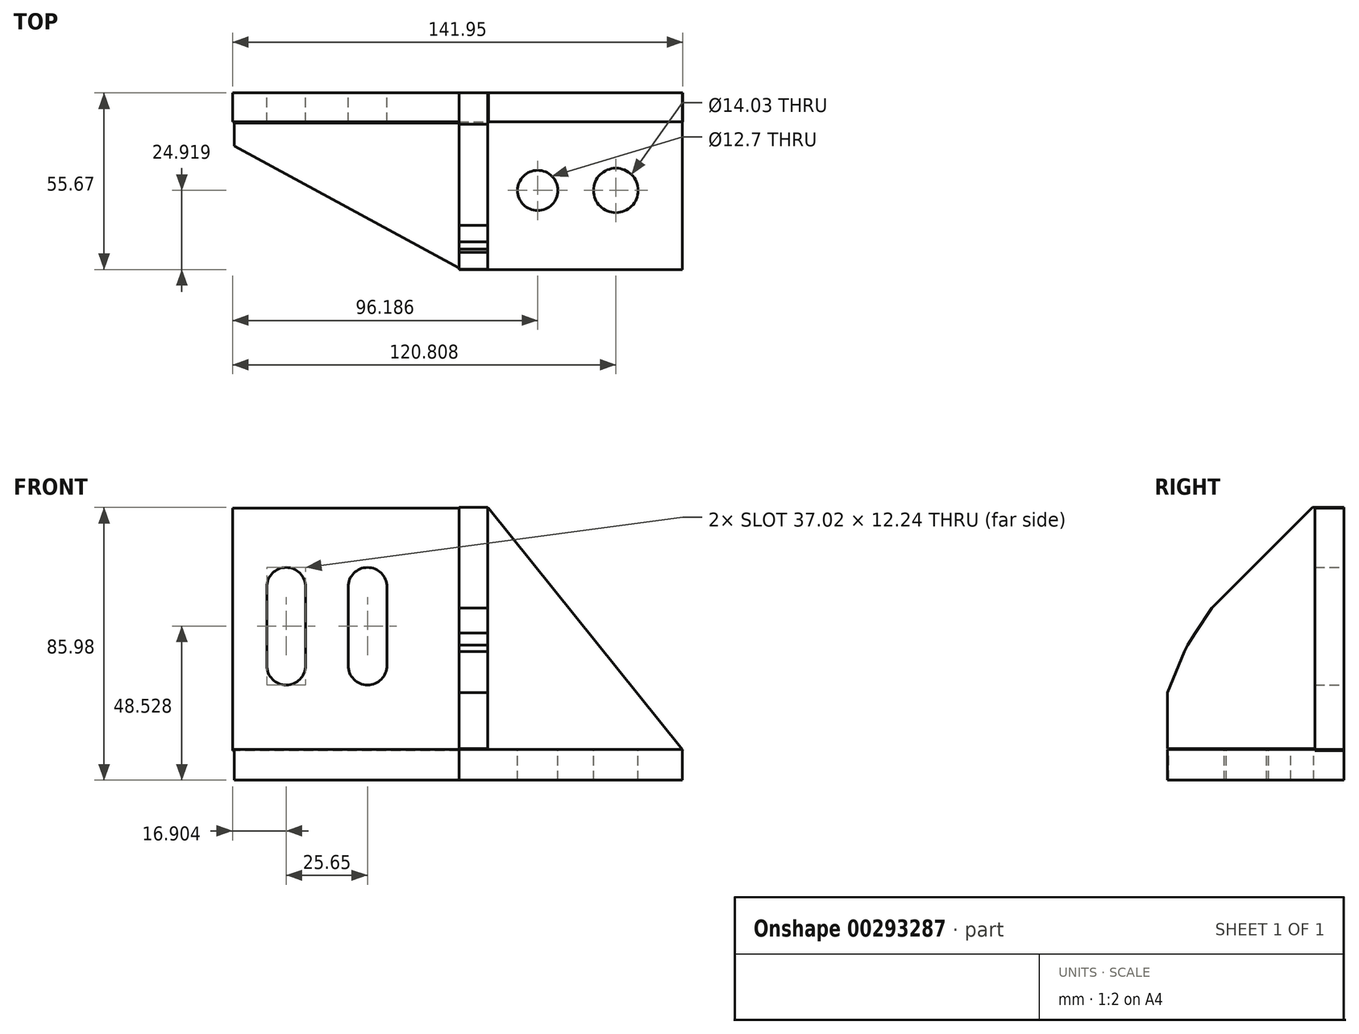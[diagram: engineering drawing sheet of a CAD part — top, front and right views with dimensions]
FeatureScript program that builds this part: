
annotation { "Feature Type Name" : "Feature", "Feature Type Description" : "" }
export const myFeature = defineFeature(function(context is Context, id is Id, definition is map)
    precondition{}
    {
        {
            var Q0;
            Q0=qCreatedBy(makeId("Front.planeOp"),FACE);
            var sketch = newSketch(context, id + "F0", { "sketchPlane" : qUnion([Q0])});
            skLineSegment(sketch, "E0.bottom", {"start": v(-71.41, 40.66) * mm, "end": v(9.33, 40.66) * mm});
            skLineSegment(sketch, "E0.top", {"start": v(-71.41, -35.7) * mm, "end": v(9.33, -35.7) * mm});
            skLineSegment(sketch, "E0.left", {"start": v(-71.41, 40.66) * mm, "end": v(-71.41, -35.7) * mm});
            skLineSegment(sketch, "E0.right", {"start": v(9.33, 40.66) * mm, "end": v(9.33, -35.7) * mm});
            skLineSegment(sketch, "E1", {"start": v(9.33, 40.66) * mm, "end": v(70.54, -35.7) * mm});
            skLineSegment(sketch, "E2", {"start": v(70.54, -35.7) * mm, "end": v(9.33, -35.7) * mm});
            skLineSegment(sketch, "E3", {"start": v(-60.63, 15.89) * mm, "end": v(-60.63, -8.9) * mm});
            skLineSegment(sketch, "E4", {"start": v(-48.38, -8.9) * mm, "end": v(-48.38, 15.89) * mm});
            skArc(sketch, "E5", {"start": v(-48.38, 15.89) * mm, "mid": v(-54.5, 22) * mm, "end": v(-60.63, 15.89) * mm});
            skArc(sketch, "E6", {"start": v(-60.63, -8.9) * mm, "mid": v(-54.5, -15.01) * mm, "end": v(-48.38, -8.9) * mm});
            skLineSegment(sketch, "E7", {"start": v(-34.98, 15.89) * mm, "end": v(-34.98, -8.9) * mm});
            skLineSegment(sketch, "E8", {"start": v(-22.74, -8.9) * mm, "end": v(-22.74, 15.89) * mm});
            skArc(sketch, "E9", {"start": v(-34.98, -8.9) * mm, "mid": v(-28.86, -15.01) * mm, "end": v(-22.74, -8.9) * mm});
            skArc(sketch, "E10", {"start": v(-22.74, 15.89) * mm, "mid": v(-28.86, 22) * mm, "end": v(-34.98, 15.89) * mm});
            skSolve(sketch);
        }
        {
            var Q0;
            Q0 = qSketchRegion(id + "F0", true);
            extrude(context, id + "F1", {"entities" : qUnion([Q0]), "depth" : 9.14 * mm});
        }
        {
            var Q0;
            Q0=qCreatedBy(makeId("Right.planeOp"),FACE);
            var sketch = newSketch(context, id + "F2", { "sketchPlane" : qUnion([Q0])});
            skLineSegment(sketch, "E11.bottom", {"start": v(0, -35.41) * mm, "end": v(-55.67, -35.41) * mm});
            skLineSegment(sketch, "E11.top", {"start": v(0, -45.03) * mm, "end": v(-55.67, -45.03) * mm});
            skLineSegment(sketch, "E11.left", {"start": v(0, -35.41) * mm, "end": v(0, -45.03) * mm});
            skLineSegment(sketch, "E11.right", {"start": v(-55.67, -35.41) * mm, "end": v(-55.67, -45.03) * mm});
            skSolve(sketch);
        }
        {
            var Q0;
            Q0 = qSketchRegion(id + "F2", true);
            extrude(context, id + "F3", {"entities" : qUnion([Q0]), "operationType" : NewBodyOperationType.ADD, "depth" : 70.36 * mm});
        }
        {
            var Q0;
            Q0=qCreatedBy(makeId("Front.planeOp"),FACE);
            var sketch = newSketch(context, id + "F4", { "sketchPlane" : qUnion([Q0])});
            skLineSegment(sketch, "E12.bottom", {"start": v(9.04, 40.95) * mm, "end": v(0, 40.95) * mm});
            skLineSegment(sketch, "E12.top", {"start": v(9.04, -35.12) * mm, "end": v(0, -35.12) * mm});
            skLineSegment(sketch, "E12.left", {"start": v(9.04, 40.95) * mm, "end": v(9.04, -35.12) * mm});
            skLineSegment(sketch, "E12.right", {"start": v(0, 40.95) * mm, "end": v(0, -35.12) * mm});
            skSolve(sketch);
        }
        {
            var Q0;
            Q0 = qSketchRegion(id + "F4", true);
            extrude(context, id + "F5", {"entities" : qUnion([Q0]), "operationType" : NewBodyOperationType.ADD, "depth" : 55.63 * mm});
        }
        {
            var Q0;
            Q0=makeQuery(id+"F5.opExtrude","CAP_EDGE",EDGE,{"disambiguationData":[OSD([sQuery(id+"F4.wireOp",EDGE,"E12.bottom")])],"isStart":false});
            chamfer(context, id + "F6", {"entities" : qUnion([Q0]), "width" : 45.72 * mm, "tangentPropagation" : true});
        }
        {
            var Q0;
            {var subQ0=sQuery(id+"F4.wireOp",EDGE,"E12.bottom");Q0=makeQuery(id+"F6.opChamfer","BLEND_EDGE",EDGE,{"blendedFrom":[makeQuery(id+"F5.opExtrude","CAP_EDGE",EDGE,{"disambiguationData":[OSD([subQ0])],"isStart":false}),makeQuery(id+"F5.opExtrude","CAP_FACE",FACE,{"disambiguationData":[OSD([subQ0,sQuery(id+"F4.wireOp",EDGE,"E12.top"),sQuery(id+"F4.wireOp",EDGE,"E12.left"),sQuery(id+"F4.wireOp",EDGE,"E12.right")])],"isStart":false})],"blendedInto":[makeQuery(id+"F5.opExtrude","CAP_FACE",FACE,{"disambiguationData":[OSD([subQ0,sQuery(id+"F4.wireOp",EDGE,"E12.top"),sQuery(id+"F4.wireOp",EDGE,"E12.left"),sQuery(id+"F4.wireOp",EDGE,"E12.right")])],"isStart":false})]});}
            chamfer(context, id + "F7", {"entities" : qUnion([Q0]), "width" : 30.48 * mm, "tangentPropagation" : true});
        }
        {
            var Q0;
            {var subQ0=sQuery(id+"F4.wireOp",EDGE,"E12.bottom");Q0=makeQuery(id+"F7.opChamfer","BLEND_EDGE",EDGE,{"blendedFrom":[makeQuery(id+"F6.opChamfer","BLEND_EDGE",EDGE,{"blendedFrom":[makeQuery(id+"F5.opExtrude","CAP_EDGE",EDGE,{"disambiguationData":[OSD([subQ0])],"isStart":false}),makeQuery(id+"F5.opExtrude","CAP_FACE",FACE,{"disambiguationData":[OSD([subQ0,sQuery(id+"F4.wireOp",EDGE,"E12.top"),sQuery(id+"F4.wireOp",EDGE,"E12.left"),sQuery(id+"F4.wireOp",EDGE,"E12.right")])],"isStart":false})],"blendedInto":[makeQuery(id+"F5.opExtrude","CAP_FACE",FACE,{"disambiguationData":[OSD([subQ0,sQuery(id+"F4.wireOp",EDGE,"E12.top"),sQuery(id+"F4.wireOp",EDGE,"E12.left"),sQuery(id+"F4.wireOp",EDGE,"E12.right")])],"isStart":false})]}),makeQuery(id+"F6.opChamfer","BLEND_FACE",FACE,{"disambiguationData":[OSD([subQ0])]})],"blendedInto":[makeQuery(id+"F6.opChamfer","BLEND_FACE",FACE,{"disambiguationData":[OSD([subQ0])]})]});}
            chamfer(context, id + "F8", {"entities" : qUnion([Q0]), "width" : 35.56 * mm, "tangentPropagation" : true});
        }
        {
            var Q0;
            {var subQ0=sQuery(id+"F4.wireOp",EDGE,"E12.right");var subQ1=sQuery(id+"F4.wireOp",EDGE,"E12.left");var subQ2=sQuery(id+"F4.wireOp",EDGE,"E12.top");var subQ3=sQuery(id+"F4.wireOp",EDGE,"E12.bottom");Q0=makeQuery(id+"F8.opChamfer","BLEND_EDGE",EDGE,{"blendedFrom":[makeQuery(id+"F7.opChamfer","BLEND_EDGE",EDGE,{"blendedFrom":[makeQuery(id+"F6.opChamfer","BLEND_EDGE",EDGE,{"blendedFrom":[makeQuery(id+"F5.opExtrude","CAP_EDGE",EDGE,{"disambiguationData":[OSD([subQ3])],"isStart":false}),makeQuery(id+"F5.opExtrude","CAP_FACE",FACE,{"disambiguationData":[OSD([subQ3,subQ2,subQ1,subQ0])],"isStart":false})],"blendedInto":[makeQuery(id+"F5.opExtrude","CAP_FACE",FACE,{"disambiguationData":[OSD([subQ3,subQ2,subQ1,subQ0])],"isStart":false})]}),makeQuery(id+"F6.opChamfer","BLEND_FACE",FACE,{"disambiguationData":[OSD([subQ3])]})],"blendedInto":[makeQuery(id+"F6.opChamfer","BLEND_FACE",FACE,{"disambiguationData":[OSD([subQ3])]})]}),makeQuery(id+"F7.opChamfer","BLEND_FACE",FACE,{"disambiguationData":[OSD([subQ3,subQ2,subQ1,subQ0])]})],"blendedInto":[makeQuery(id+"F7.opChamfer","BLEND_FACE",FACE,{"disambiguationData":[OSD([subQ3,subQ2,subQ1,subQ0])]})]});}
            chamfer(context, id + "F9", {"entities" : qUnion([Q0]), "width" : 22.86 * mm, "tangentPropagation" : true});
        }
        {
            var Q0;
            {var subQ0=sQuery(id+"F4.wireOp",EDGE,"E12.right");var subQ1=sQuery(id+"F4.wireOp",EDGE,"E12.left");var subQ2=sQuery(id+"F4.wireOp",EDGE,"E12.top");var subQ3=sQuery(id+"F4.wireOp",EDGE,"E12.bottom");Q0=makeQuery(id+"F9.opChamfer","BLEND_EDGE",EDGE,{"blendedFrom":[makeQuery(id+"F8.opChamfer","BLEND_EDGE",EDGE,{"blendedFrom":[makeQuery(id+"F7.opChamfer","BLEND_EDGE",EDGE,{"blendedFrom":[makeQuery(id+"F6.opChamfer","BLEND_EDGE",EDGE,{"blendedFrom":[makeQuery(id+"F5.opExtrude","CAP_EDGE",EDGE,{"disambiguationData":[OSD([subQ3])],"isStart":false}),makeQuery(id+"F5.opExtrude","CAP_FACE",FACE,{"disambiguationData":[OSD([subQ3,subQ2,subQ1,subQ0])],"isStart":false})],"blendedInto":[makeQuery(id+"F5.opExtrude","CAP_FACE",FACE,{"disambiguationData":[OSD([subQ3,subQ2,subQ1,subQ0])],"isStart":false})]}),makeQuery(id+"F6.opChamfer","BLEND_FACE",FACE,{"disambiguationData":[OSD([subQ3])]})],"blendedInto":[makeQuery(id+"F6.opChamfer","BLEND_FACE",FACE,{"disambiguationData":[OSD([subQ3])]})]}),makeQuery(id+"F7.opChamfer","BLEND_FACE",FACE,{"disambiguationData":[OSD([subQ3,subQ2,subQ1,subQ0])]})],"blendedInto":[makeQuery(id+"F7.opChamfer","BLEND_FACE",FACE,{"disambiguationData":[OSD([subQ3,subQ2,subQ1,subQ0])]})]}),makeQuery(id+"F8.opChamfer","BLEND_FACE",FACE,{"disambiguationData":[OSD([subQ3,subQ2,subQ1,subQ0])]})],"blendedInto":[makeQuery(id+"F8.opChamfer","BLEND_FACE",FACE,{"disambiguationData":[OSD([subQ3,subQ2,subQ1,subQ0])]})]});}
            chamfer(context, id + "F10", {"entities" : qUnion([Q0]), "width" : 45.72 * mm, "tangentPropagation" : true});
        }
        {
            var Q0;
            Q0=qCreatedBy(makeId("Top.planeOp"),FACE);
            var sketch = newSketch(context, id + "F11", { "sketchPlane" : qUnion([Q0])});
            skLineSegment(sketch, "E13", {"start": v(0, -55.23) * mm, "end": v(-70.83, -16.76) * mm});
            skLineSegment(sketch, "E14", {"start": v(-70.83, -16.76) * mm, "end": v(-70.83, -9.47) * mm});
            skLineSegment(sketch, "E15", {"start": v(-70.83, -9.47) * mm, "end": v(0, -9.47) * mm});
            skLineSegment(sketch, "E16", {"start": v(0, -9.47) * mm, "end": v(0, -55.23) * mm});
            skSolve(sketch);
        }
        {
            var Q0;
            Q0 = qSketchRegion(id + "F11", true);
            extrude(context, id + "F12", {"entities" : qUnion([Q0]), "operationType" : NewBodyOperationType.ADD, "oppositeDirection" : true, "depth" : 44.96 * mm});
        }
        {
            var Q0;
            Q0=qCreatedBy(makeId("Top.planeOp"),FACE);
            var sketch = newSketch(context, id + "F13", { "sketchPlane" : qUnion([Q0])});
            skLineSegment(sketch, "E17", {"start": v(-71.41, -9.18) * mm, "end": v(-71.41, -16.47) * mm});
            skLineSegment(sketch, "E18", {"start": v(-71.41, -16.47) * mm, "end": v(0, -55.82) * mm});
            skLineSegment(sketch, "E19", {"start": v(0, -55.82) * mm, "end": v(0, -9.18) * mm});
            skLineSegment(sketch, "E20", {"start": v(0, -9.18) * mm, "end": v(-71.41, -9.18) * mm});
            skSolve(sketch);
        }
        {
            var Q0;
            Q0 = qSketchRegion(id + "F13", true);
            extrude(context, id + "F14", {"entities" : qUnion([Q0]), "operationType" : NewBodyOperationType.REMOVE, "oppositeDirection" : true, "depth" : 35.3 * mm});
        }
        {
            var Q0;
            Q0=qCreatedBy(makeId("Top.planeOp"),FACE);
            var sketch = newSketch(context, id + "F15", { "sketchPlane" : qUnion([Q0])});
            skCircle(sketch, "E21", {"center": v(24.78, -30.75) * mm, "radius": 6.35 * mm});
            skCircle(sketch, "E22", {"center": v(49.4, -30.75) * mm, "radius": 7.02 * mm});
            skSolve(sketch);
        }
        {
            var Q0;
            Q0 = qSketchRegion(id + "F15", true);
            extrude(context, id + "F16", {"entities" : qUnion([Q0]), "operationType" : NewBodyOperationType.REMOVE, "oppositeDirection" : true, "depth" : 55.37 * mm});
        }
    });
